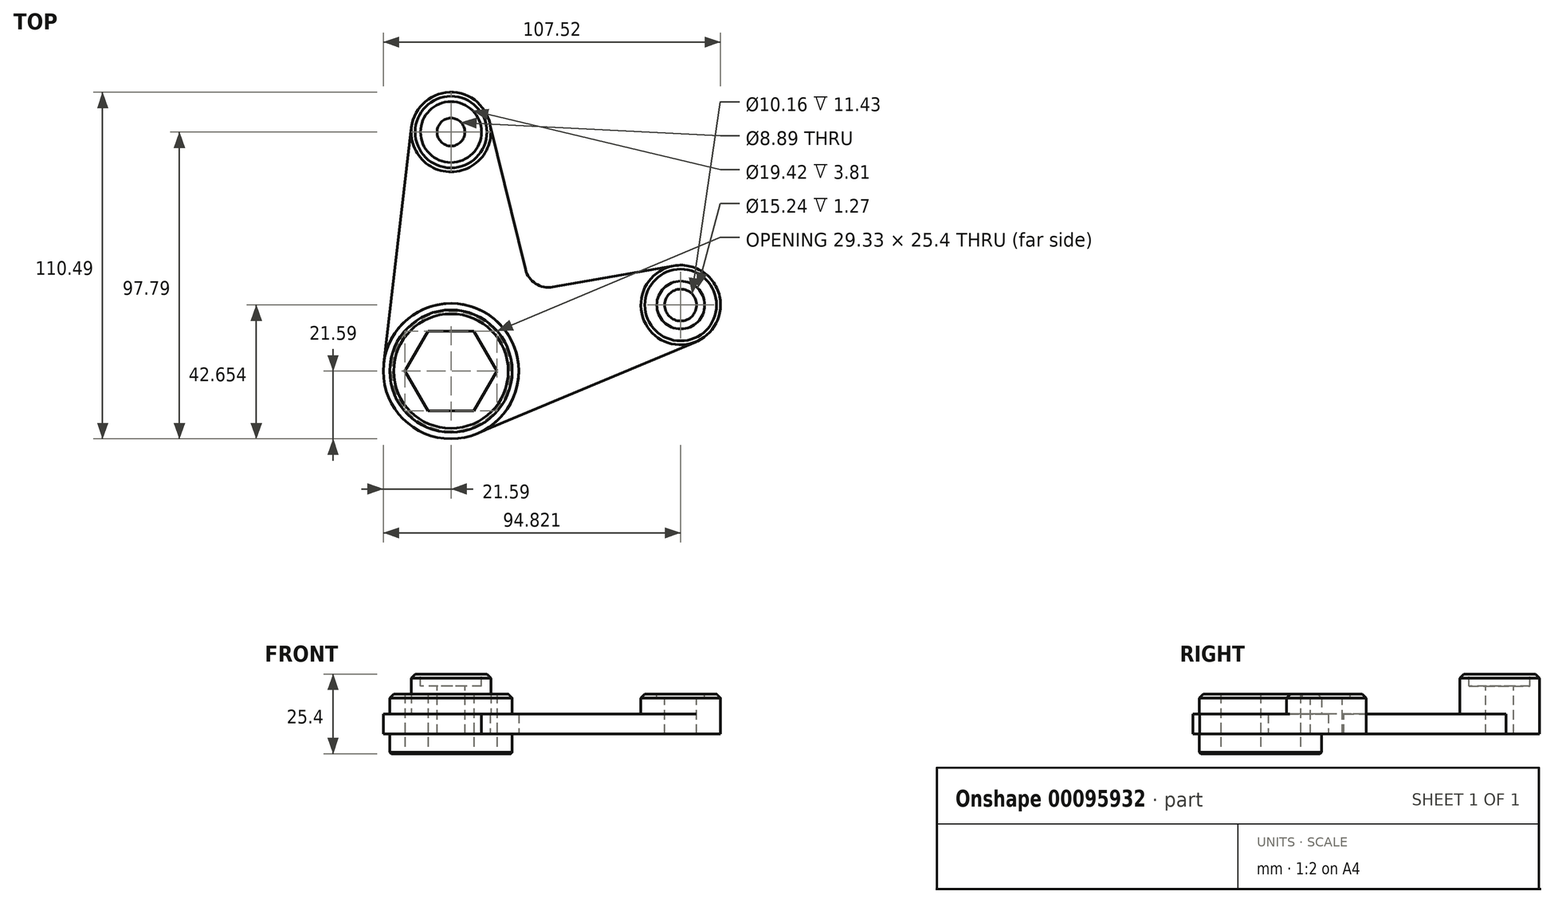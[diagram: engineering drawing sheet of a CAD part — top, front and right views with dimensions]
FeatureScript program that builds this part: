
annotation { "Feature Type Name" : "Feature", "Feature Type Description" : "" }
export const myFeature = defineFeature(function(context is Context, id is Id, definition is map)
    precondition{}
    {
        {
            var Q0;
            Q0=qCreatedBy(makeId("Top.planeOp"),FACE);
            var sketch = newSketch(context, id + "F0", { "sketchPlane" : qUnion([Q0])});
            skCircle(sketch, "E0", {"center": v(0, 76.2) * mm, "radius": 12.7 * mm});
            skCircle(sketch, "E1", {"center": v(0, 0) * mm, "radius": 21.59 * mm});
            skLineSegment(sketch, "E2", {"start": v(-12.61, 77.68) * mm, "end": v(-21.44, 2.52) * mm});
            skCircle(sketch, "E3.cCircle", {"center": v(0, 0) * mm, "radius": 12.7 * mm, "construction": true});
            skLineSegment(sketch, "E3.0", {"start": v(-7.33, 12.7) * mm, "end": v(7.33, 12.7) * mm});
            skLineSegment(sketch, "E3.1", {"start": v(7.33, 12.7) * mm, "end": v(14.66, 0) * mm});
            skLineSegment(sketch, "E3.2", {"start": v(14.66, 0) * mm, "end": v(7.33, -12.7) * mm});
            skLineSegment(sketch, "E3.3", {"start": v(7.33, -12.7) * mm, "end": v(-7.33, -12.7) * mm});
            skLineSegment(sketch, "E3.4", {"start": v(-7.33, -12.7) * mm, "end": v(-14.66, 0) * mm});
            skLineSegment(sketch, "E3.5", {"start": v(-14.66, 0) * mm, "end": v(-7.33, 12.7) * mm});
            skPoint(sketch, "E3.0.midPoint", {"position": v(0, 12.7) * mm});
            skPoint(sketch, "E4.trimOffspring.end.orphan", {"position": v(0, 25.76) * mm});
            skLineSegment(sketch, "E5", {"start": v(12.52, 78.32) * mm, "end": v(25.44, 25.54) * mm});
            skCircle(sketch, "E6", {"center": v(73.23, 21.06) * mm, "radius": 12.7 * mm});
            skLineSegment(sketch, "E7", {"start": v(25.44, 25.54) * mm, "end": v(71.03, 33.57) * mm});
            skLineSegment(sketch, "E8", {"start": v(9.64, -19.32) * mm, "end": v(78.13, 9.35) * mm});
            skCircle(sketch, "E9", {"center": v(0, 0) * mm, "radius": 19.52 * mm});
            skSolve(sketch);
        }
        {
            var Q0;
            {var subQ0=sQuery(id+"F0.wireOp",EDGE,"E2");Q0=makeQuery(id+"F0.imprint","IMPRINT",FACE,{"disambiguationData":[TD([[makeQuery(id+"F0.imprint","IMPRINT",EDGE,{"derivedFrom":subQ0}),1.0]])]});}
            extrude(context, id + "F1", {"entities" : qUnion([Q0]), "depth" : 6.35 * mm});
        }
        {
            var Q0;
            Q0=makeQuery(id+"F0.imprint","IMPRINT",FACE,{"disambiguationData":[TD([[makeQuery(id+"F0.imprint","IMPRINT",EDGE,{"derivedFrom":sQuery(id+"F0.wireOp",EDGE,"E3.0")}),1.0]])]});
            var Q1;
            {var subQ0=sQuery(id+"F0.wireOp",EDGE,"E0");var subQ1=makeQuery(id+"F0.imprint","INTERSECT",VERTEX,{"derivedFrom":[subQ0,sQuery(id+"F0.wireOp",EDGE,"E2")]});Q1=makeQuery(id+"F0.imprint","IMPRINT",FACE,{"disambiguationData":[TD([[makeQuery(id+"F0.imprint","IMPRINT",EDGE,{"disambiguationData":[TD([[subQ1,1.0]])],"derivedFrom":subQ0}),1.0]])]});}
            var Q2;
            {var subQ0=sQuery(id+"F0.wireOp",EDGE,"UCbb1fUN-bQ2s-U6LD-SMtF-A29RtSXV32oS");var subQ1=makeQuery(id+"F0.imprint","INTERSECT",VERTEX,{"derivedFrom":[subQ0,sQuery(id+"F0.wireOp",EDGE,"2wVTPmc6-2JMl-f3f1-XjNG-VOtBA7JF05Rc")]});Q2=makeQuery(id+"F0.imprint","IMPRINT",FACE,{"disambiguationData":[TD([[makeQuery(id+"F0.imprint","IMPRINT",EDGE,{"disambiguationData":[TD([[subQ1,-1.0]])],"derivedFrom":subQ0}),1.0]])]});}
            extrude(context, id + "F2", {"entities" : qUnion([Q0, Q1, Q2]), "operationType" : NewBodyOperationType.ADD, "depth" : 12.7 * mm});
        }
        {
            var Q0;
            Q0=makeQuery(id+"F2.opExtrude","CAP_FACE",FACE,{"disambiguationData":[OSD([sQuery(id+"F0.wireOp",EDGE,"E0")])],"isStart":false});
            extrude(context, id + "F3", {"entities" : qUnion([Q0]), "operationType" : NewBodyOperationType.ADD, "depth" : 6.35 * mm});
        }
        {
            var Q0;
            {var subQ0=sQuery(id+"F0.wireOp",EDGE,"E6");var subQ1=makeQuery(id+"F0.imprint","INTERSECT",VERTEX,{"derivedFrom":[subQ0,sQuery(id+"F0.wireOp",EDGE,"E7")]});Q0=makeQuery(id+"F0.imprint","IMPRINT",FACE,{"disambiguationData":[TD([[makeQuery(id+"F0.imprint","IMPRINT",EDGE,{"disambiguationData":[TD([[subQ1,-1.0]])],"derivedFrom":subQ0}),1.0]])]});}
            extrude(context, id + "F4", {"entities" : qUnion([Q0]), "operationType" : NewBodyOperationType.ADD, "depth" : 12.7 * mm});
        }
        {
            var Q0;
            Q0=makeQuery(id+"F2.opExtrude","CAP_EDGE",EDGE,{"disambiguationData":[OSD([sQuery(id+"F0.wireOp",EDGE,"E1")])],"isStart":false});
            var Q1;
            Q1=makeQuery(id+"F3.opExtrude","CAP_EDGE",EDGE,{"disambiguationData":[OSD([sQuery(id+"F0.wireOp",EDGE,"E0")])],"isStart":false});
            var Q2;
            Q2=makeQuery(id+"F4.opExtrude","CAP_EDGE",EDGE,{"disambiguationData":[OSD([sQuery(id+"F0.wireOp",EDGE,"E6")])],"isStart":false});
            var Q3;
            Q3=makeQuery(id+"F2.opExtrude","CAP_EDGE",EDGE,{"disambiguationData":[OSD([sQuery(id+"F0.wireOp",EDGE,"E9")])],"isStart":false});
            chamfer(context, id + "F5", {"entities" : qUnion([Q0, Q1, Q2, Q3]), "width" : 1.27 * mm, "tangentPropagation" : true});
        }
        {
            var Q0;
            Q0=makeQuery(id+"F3.opExtrude","CAP_FACE",FACE,{"disambiguationData":[OSD([sQuery(id+"F0.wireOp",EDGE,"E0")])],"isStart":false});
            var sketch = newSketch(context, id + "F6", { "sketchPlane" : qUnion([Q0])});
            skCircle(sketch, "E10", {"center": v(0, 76.2) * mm, "radius": 4.45 * mm});
            skSolve(sketch);
        }
        {
            var Q0;
            Q0 = qSketchRegion(id + "F6", true);
            extrude(context, id + "F7", {"entities" : qUnion([Q0]), "operationType" : NewBodyOperationType.REMOVE, "oppositeDirection" : true, "depth" : 25.4 * mm});
        }
        {
            var Q0;
            Q0=makeQuery(id+"F3.opExtrude","CAP_FACE",FACE,{"disambiguationData":[OSD([sQuery(id+"F0.wireOp",EDGE,"E0")])],"isStart":false});
            var sketch = newSketch(context, id + "F8", { "sketchPlane" : qUnion([Q0])});
            skCircle(sketch, "E11", {"center": v(0, 76.2) * mm, "radius": 9.7 * mm});
            skSolve(sketch);
        }
        {
            var Q0;
            Q0 = qSketchRegion(id + "F8", true);
            extrude(context, id + "F9", {"entities" : qUnion([Q0]), "operationType" : NewBodyOperationType.REMOVE, "oppositeDirection" : true, "depth" : 3.8 * mm});
        }
        {
            var Q0;
            Q0=makeQuery(id+"F4.opExtrude","CAP_FACE",FACE,{"disambiguationData":[OSD([sQuery(id+"F0.wireOp",EDGE,"E6")])],"isStart":false});
            var sketch = newSketch(context, id + "F10", { "sketchPlane" : qUnion([Q0])});
            skCircle(sketch, "E12", {"center": v(73.23, 21.06) * mm, "radius": 5.08 * mm});
            skCircle(sketch, "E13", {"center": v(73.23, 21.06) * mm, "radius": 7.62 * mm});
            skSolve(sketch);
        }
        {
            var Q0;
            Q0=makeQuery(id+"F10.imprint","IMPRINT",FACE,{"disambiguationData":[TD([[makeQuery(id+"F10.imprint","IMPRINT",EDGE,{"derivedFrom":sQuery(id+"F10.wireOp",EDGE,"E12")}),1.0]])]});
            extrude(context, id + "F11", {"entities" : qUnion([Q0]), "operationType" : NewBodyOperationType.REMOVE, "oppositeDirection" : true, "depth" : 25.4 * mm});
        }
        {
            var Q0;
            Q0=makeQuery(id+"F10.imprint","IMPRINT",FACE,{"disambiguationData":[TD([[makeQuery(id+"F10.imprint","IMPRINT",EDGE,{"derivedFrom":sQuery(id+"F10.wireOp",EDGE,"E12")}),-1.0]])]});
            extrude(context, id + "F12", {"entities" : qUnion([Q0]), "operationType" : NewBodyOperationType.REMOVE, "oppositeDirection" : true, "depth" : 1.27 * mm});
        }
        {
            var Q0;
            Q0=makeQuery(id+"F0.imprint","IMPRINT",FACE,{"disambiguationData":[TD([[makeQuery(id+"F0.imprint","IMPRINT",EDGE,{"derivedFrom":sQuery(id+"F0.wireOp",EDGE,"E9")}),-1.0]])]});
            extrude(context, id + "F13", {"entities" : qUnion([Q0]), "depth" : 6.35 * mm});
        }
        {
            var Q0;
            Q0=makeQuery(id+"F2.opExtrude","CAP_FACE",FACE,{"disambiguationData":[OSD([sQuery(id+"F0.wireOp",EDGE,"E3.0"),sQuery(id+"F0.wireOp",EDGE,"E3.1"),sQuery(id+"F0.wireOp",EDGE,"E3.2"),sQuery(id+"F0.wireOp",EDGE,"E3.3"),sQuery(id+"F0.wireOp",EDGE,"E3.4"),sQuery(id+"F0.wireOp",EDGE,"E3.5"),sQuery(id+"F0.wireOp",EDGE,"E9")])],"isStart":true});
            extrude(context, id + "F14", {"entities" : qUnion([Q0]), "operationType" : NewBodyOperationType.ADD, "depth" : 6.35 * mm});
        }
        {
            var Q0;
            Q0=makeQuery(id+"F1.opExtrude","SWEPT_EDGE",EDGE,{"disambiguationData":[OSD([sQuery(id+"F0.wireOp",EDGE,"E5"),sQuery(id+"F0.wireOp",EDGE,"E7")])]});
            fillet(context, id + "F15", {"entities" : qUnion([Q0]), "radius" : 7.62 * mm, "tangentPropagation" : true, "allowEdgeOverflow" : false});
        }
        {
            var Q0;
            Q0=makeQuery(id+"F14.opExtrude","CAP_EDGE",EDGE,{"disambiguationData":[OSD([sQuery(id+"F0.wireOp",EDGE,"E9")])],"isStart":false});
            chamfer(context, id + "F16", {"entities" : qUnion([Q0]), "width" : 0.5 * mm, "tangentPropagation" : true});
        }
    });
